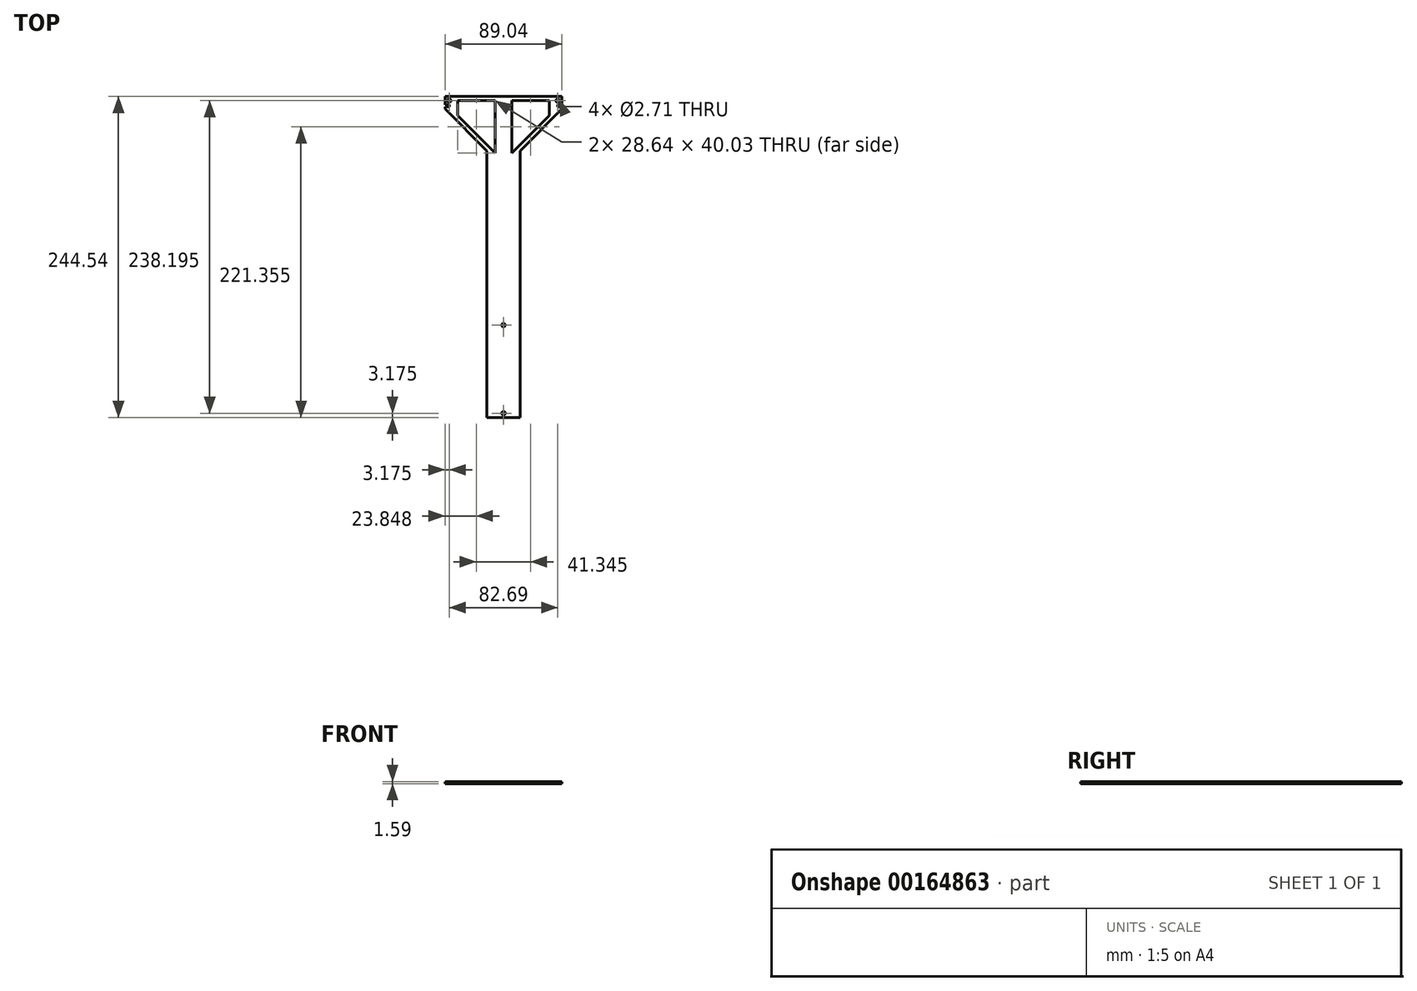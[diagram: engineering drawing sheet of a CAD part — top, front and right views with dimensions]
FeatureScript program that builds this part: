
annotation { "Feature Type Name" : "Feature", "Feature Type Description" : "" }
export const myFeature = defineFeature(function(context is Context, id is Id, definition is map)
    precondition{}
    {
        {
            var Q0;
            Q0=qCreatedBy(makeId("Top.planeOp"),FACE);
            var sketch = newSketch(context, id + "F0", { "sketchPlane" : qUnion([Q0])});
            skLineSegment(sketch, "E0.bottom", {"start": v(0, 0) * mm, "end": v(25.4, 0) * mm, "construction": true});
            skLineSegment(sketch, "E0.top", {"start": v(0, -203.2) * mm, "end": v(25.4, -203.2) * mm});
            skLineSegment(sketch, "E0.left", {"start": v(0, 0) * mm, "end": v(0, -203.2) * mm});
            skLineSegment(sketch, "E0.right", {"start": v(25.4, 0) * mm, "end": v(25.4, -203.2) * mm});
            skLineSegment(sketch, "E1", {"start": v(12.7, -132.9) * mm, "end": v(12.7, -200.03) * mm, "construction": true});
            skCircle(sketch, "E2", {"center": v(12.7, -132.9) * mm, "radius": 1.35 * mm});
            skCircle(sketch, "E3", {"center": v(12.7, -200.03) * mm, "radius": 1.35 * mm});
            skLineSegment(sketch, "E4", {"start": v(12.7, -200.03) * mm, "end": v(12.7, -203.2) * mm, "construction": true});
            skLineSegment(sketch, "E5", {"start": v(12.7, 0) * mm, "end": v(12.7, 38.17) * mm, "construction": true});
            skLineSegment(sketch, "E6", {"start": v(-28.64, 38.17) * mm, "end": v(54.04, 38.17) * mm, "construction": true});
            skCircle(sketch, "E7", {"center": v(-28.64, 38.17) * mm, "radius": 1.35 * mm});
            skCircle(sketch, "E8", {"center": v(54.04, 38.17) * mm, "radius": 1.35 * mm});
            skLineSegment(sketch, "E9", {"start": v(0, 0) * mm, "end": v(-31.82, 31.82) * mm});
            skLineSegment(sketch, "E10", {"start": v(-31.82, 31.82) * mm, "end": v(-31.82, 41.34) * mm});
            skLineSegment(sketch, "E11", {"start": v(-31.82, 41.34) * mm, "end": v(57.22, 41.34) * mm});
            skLineSegment(sketch, "E12", {"start": v(57.22, 41.34) * mm, "end": v(57.22, 31.82) * mm});
            skLineSegment(sketch, "E13", {"start": v(57.22, 31.82) * mm, "end": v(25.4, 0) * mm});
            skLineSegment(sketch, "E14", {"start": v(-28.64, 38.17) * mm, "end": v(-28.64, 31.82) * mm, "construction": true});
            skLineSegment(sketch, "E15", {"start": v(-28.64, 31.82) * mm, "end": v(-31.82, 31.82) * mm, "construction": true});
            skLineSegment(sketch, "E16", {"start": v(12.7, 38.17) * mm, "end": v(12.7, 41.34) * mm, "construction": true});
            skSolve(sketch);
        }
        {
            var Q0;
            Q0=qSketchRegion(id+"F0",true);
            extrude(context, id + "F1", {"entities" : qUnion([Q0]), "depth" : 1.59 * mm});
        }
        {
            var Q0;
            Q0=makeQuery(id+"F1.opExtrude","CAP_FACE",FACE,{"disambiguationData":[OSD([sQuery(id+"F0.wireOp",EDGE,"E0.top"),sQuery(id+"F0.wireOp",EDGE,"E0.left"),sQuery(id+"F0.wireOp",EDGE,"E0.right"),sQuery(id+"F0.wireOp",EDGE,"E2"),sQuery(id+"F0.wireOp",EDGE,"E3"),sQuery(id+"F0.wireOp",EDGE,"E7"),sQuery(id+"F0.wireOp",EDGE,"E8"),sQuery(id+"F0.wireOp",EDGE,"E9"),sQuery(id+"F0.wireOp",EDGE,"E10"),sQuery(id+"F0.wireOp",EDGE,"E11"),sQuery(id+"F0.wireOp",EDGE,"E12"),sQuery(id+"F0.wireOp",EDGE,"E13")])],"isStart":false});
            var sketch = newSketch(context, id + "F2", { "sketchPlane" : qUnion([Q0])});
            skLineSegment(sketch, "E17.bottom", {"start": v(-31.82, 35) * mm, "end": v(-28.64, 35) * mm});
            skLineSegment(sketch, "E17.top", {"start": v(-31.82, 33.4) * mm, "end": v(-28.64, 33.4) * mm});
            skLineSegment(sketch, "E17.left", {"start": v(-31.82, 35) * mm, "end": v(-31.82, 33.4) * mm});
            skLineSegment(sketch, "E17.right", {"start": v(-28.64, 35) * mm, "end": v(-28.64, 33.4) * mm});
            skLineSegment(sketch, "E18.bottom", {"start": v(57.22, 35) * mm, "end": v(54.04, 35) * mm});
            skLineSegment(sketch, "E18.top", {"start": v(57.22, 33.4) * mm, "end": v(54.04, 33.4) * mm});
            skLineSegment(sketch, "E18.left", {"start": v(57.22, 35) * mm, "end": v(57.22, 33.4) * mm});
            skLineSegment(sketch, "E18.right", {"start": v(54.04, 35) * mm, "end": v(54.04, 33.4) * mm});
            skLineSegment(sketch, "E19", {"start": v(-28.64, 35) * mm, "end": v(-28.64, 38.17) * mm, "construction": true});
            skLineSegment(sketch, "E20", {"start": v(12.7, 41.34) * mm, "end": v(12.7, 38.17) * mm, "construction": true});
            skLineSegment(sketch, "E21", {"start": v(-15.9, 15.9) * mm, "end": v(-13.66, 18.15) * mm, "construction": true});
            skLineSegment(sketch, "E22", {"start": v(41.3, 15.9) * mm, "end": v(39.06, 18.15) * mm, "construction": true});
            skLineSegment(sketch, "E23", {"start": v(6.35, 38.17) * mm, "end": v(19.05, 38.17) * mm, "construction": true});
            skLineSegment(sketch, "E24", {"start": v(-22.3, 26.78) * mm, "end": v(6.35, -1.86) * mm});
            skLineSegment(sketch, "E25", {"start": v(6.35, -1.86) * mm, "end": v(6.35, 38.17) * mm});
            skLineSegment(sketch, "E26", {"start": v(6.35, 38.17) * mm, "end": v(-22.3, 38.17) * mm});
            skLineSegment(sketch, "E27", {"start": v(-22.3, 38.17) * mm, "end": v(-22.3, 26.78) * mm});
            skLineSegment(sketch, "E28", {"start": v(-28.64, 38.17) * mm, "end": v(-22.3, 38.17) * mm, "construction": true});
            skLineSegment(sketch, "E29", {"start": v(19.05, 38.17) * mm, "end": v(19.05, -1.86) * mm});
            skLineSegment(sketch, "E30", {"start": v(19.05, -1.86) * mm, "end": v(47.7, 26.78) * mm});
            skLineSegment(sketch, "E31", {"start": v(47.7, 26.78) * mm, "end": v(47.7, 38.17) * mm});
            skLineSegment(sketch, "E32", {"start": v(47.7, 38.17) * mm, "end": v(19.05, 38.17) * mm});
            skSolve(sketch);
        }
        {
            var Q0;
            Q0=qSketchRegion(id+"F2",true);
            var Q1;
            Q1=makeQuery(id+"F1.opExtrude","CAP_FACE",FACE,{"disambiguationData":[OSD([sQuery(id+"F0.wireOp",EDGE,"E0.top"),sQuery(id+"F0.wireOp",EDGE,"E0.left"),sQuery(id+"F0.wireOp",EDGE,"E0.right"),sQuery(id+"F0.wireOp",EDGE,"E2"),sQuery(id+"F0.wireOp",EDGE,"E3"),sQuery(id+"F0.wireOp",EDGE,"E7"),sQuery(id+"F0.wireOp",EDGE,"E8"),sQuery(id+"F0.wireOp",EDGE,"E9"),sQuery(id+"F0.wireOp",EDGE,"E10"),sQuery(id+"F0.wireOp",EDGE,"E11"),sQuery(id+"F0.wireOp",EDGE,"E12"),sQuery(id+"F0.wireOp",EDGE,"E13")])],"isStart":true});
            extrude(context, id + "F3", {"entities" : qUnion([Q0]), "operationType" : NewBodyOperationType.REMOVE, "endBound" : BoundingType.UP_TO_SURFACE, "oppositeDirection" : true, "endBoundEntityFace" : qUnion([Q1]), "depth" : 25.4 * mm});
        }
    });
